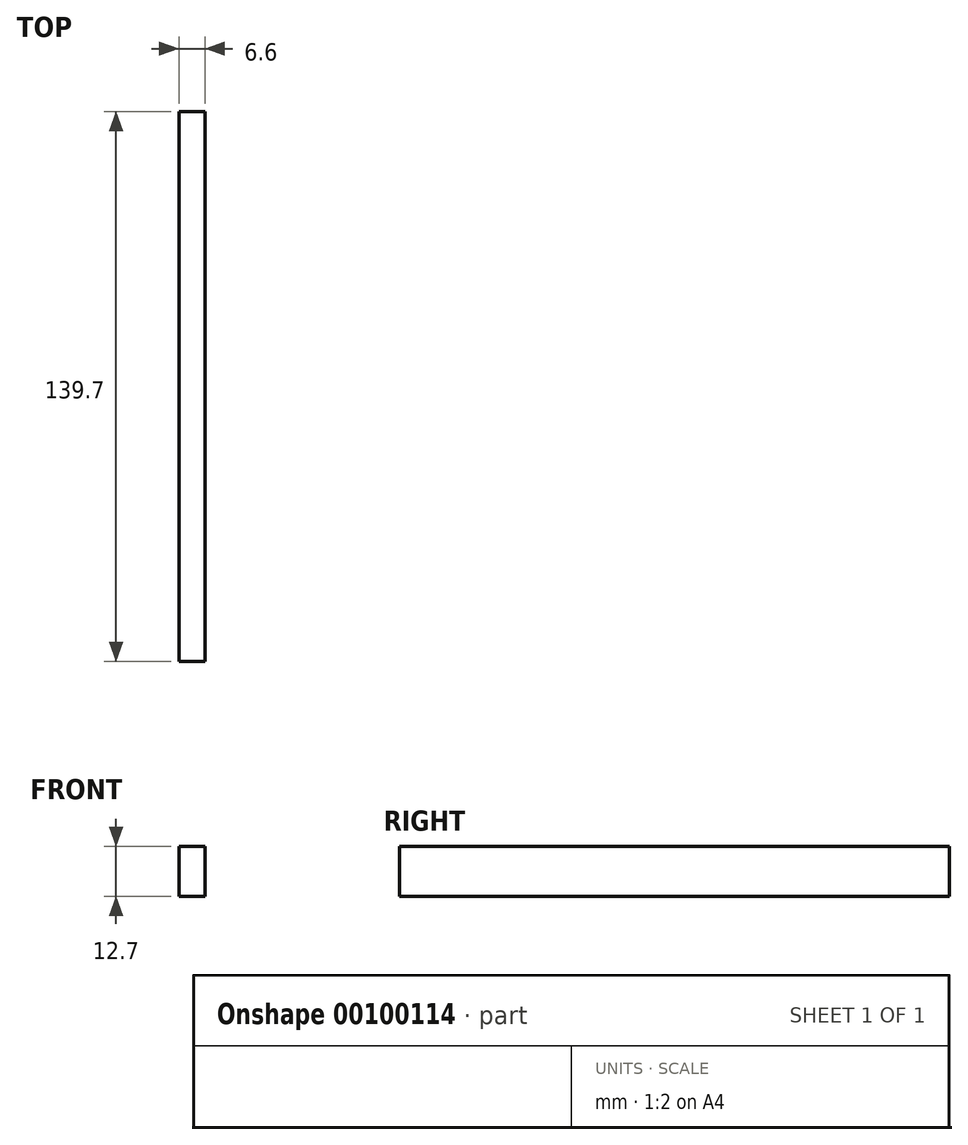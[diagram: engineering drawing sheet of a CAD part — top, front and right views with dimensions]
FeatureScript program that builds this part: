
annotation { "Feature Type Name" : "Feature", "Feature Type Description" : "" }
export const myFeature = defineFeature(function(context is Context, id is Id, definition is map)
    precondition{}
    {
        {
            var Q0;
            Q0=qCreatedBy(makeId("Front.planeOp"),FACE);
            var sketch = newSketch(context, id + "F0", { "sketchPlane" : qUnion([Q0])});
            skLineSegment(sketch, "E0.bottom", {"start": v(3.3, -6.35) * mm, "end": v(-3.3, -6.35) * mm});
            skLineSegment(sketch, "E0.top", {"start": v(3.3, 6.35) * mm, "end": v(-3.3, 6.35) * mm});
            skLineSegment(sketch, "E0.left", {"start": v(3.3, -6.35) * mm, "end": v(3.3, 6.35) * mm});
            skLineSegment(sketch, "E0.right", {"start": v(-3.3, -6.35) * mm, "end": v(-3.3, 6.35) * mm});
            skPoint(sketch, "E0.middle", {"position": v(0, 0) * mm});
            skSolve(sketch);
        }
        {
            var Q0;
            Q0 = qSketchRegion(id + "F0", true);
            extrude(context, id + "F1", {"entities" : qUnion([Q0]), "depth" : 139.7 * mm, "symmetric" : true});
        }
    });
